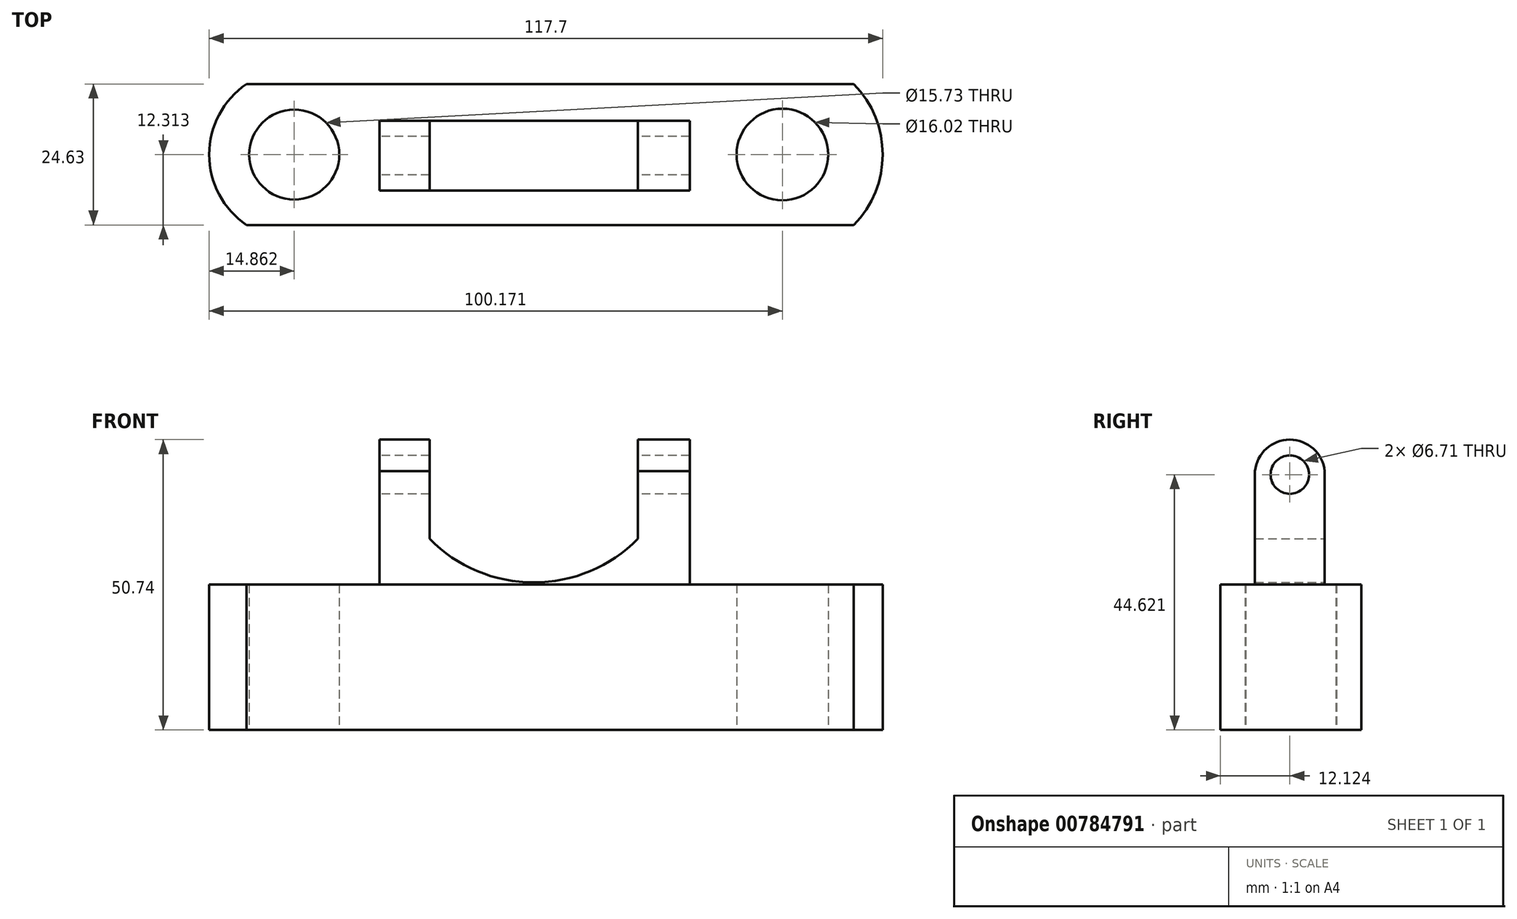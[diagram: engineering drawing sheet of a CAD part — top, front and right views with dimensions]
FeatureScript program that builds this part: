
annotation { "Feature Type Name" : "Feature", "Feature Type Description" : "" }
export const myFeature = defineFeature(function(context is Context, id is Id, definition is map)
    precondition{}
    {
        {
            var Q0;
            Q0=qCreatedBy(makeId("Top.planeOp"),FACE);
            var sketch = newSketch(context, id + "F0", { "sketchPlane" : qUnion([Q0])});
            skLineSegment(sketch, "E0", {"start": v(-47.53, -24.63) * mm, "end": v(58.57, -24.63) * mm});
            skLineSegment(sketch, "E1", {"start": v(-47.53, 0) * mm, "end": v(58.57, 0) * mm});
            skArc(sketch, "E2", {"start": v(-47.53, 0) * mm, "mid": v(-54.07, -12.32) * mm, "end": v(-47.53, -24.63) * mm});
            skArc(sketch, "E3", {"start": v(58.57, -24.63) * mm, "mid": v(63.63, -12.32) * mm, "end": v(58.57, 0) * mm});
            skCircle(sketch, "E4", {"center": v(-39.2, -12.32) * mm, "radius": 7.87 * mm});
            skCircle(sketch, "E5", {"center": v(46.1, -12.32) * mm, "radius": 8 * mm});
            skSolve(sketch);
        }
        {
            var Q0;
            Q0=makeQuery(id+"F0.imprint","IMPRINT",FACE,{"disambiguationData":[TD([[makeQuery(id+"F0.imprint","IMPRINT",EDGE,{"derivedFrom":sQuery(id+"F0.wireOp",EDGE,"E0")}),1.0]])]});
            extrude(context, id + "F1", {"entities" : qUnion([Q0]), "depth" : 25.4 * mm, "offsetDistance" : 25.4 * mm});
        }
        {
            var Q0;
            Q0=makeQuery(id+"F1.opExtrude","CAP_FACE",FACE,{"disambiguationData":[OSD([sQuery(id+"F0.wireOp",EDGE,"E0"),sQuery(id+"F0.wireOp",EDGE,"E1"),sQuery(id+"F0.wireOp",EDGE,"E2"),sQuery(id+"F0.wireOp",EDGE,"E3"),sQuery(id+"F0.wireOp",EDGE,"E4"),sQuery(id+"F0.wireOp",EDGE,"E5")])],"isStart":false});
            var sketch = newSketch(context, id + "F2", { "sketchPlane" : qUnion([Q0])});
            skLineSegment(sketch, "E6.bottom", {"start": v(-24.32, -6.42) * mm, "end": v(29.91, -6.42) * mm});
            skLineSegment(sketch, "E6.top", {"start": v(-24.32, -18.6) * mm, "end": v(29.91, -18.6) * mm});
            skLineSegment(sketch, "E6.left", {"start": v(-24.32, -6.42) * mm, "end": v(-24.32, -18.6) * mm});
            skLineSegment(sketch, "E6.right", {"start": v(29.91, -6.42) * mm, "end": v(29.91, -18.6) * mm});
            skSolve(sketch);
        }
        {
            var Q0;
            Q0=makeQuery(id+"F2.imprint","IMPRINT",FACE,{"disambiguationData":[TD([[makeQuery(id+"F2.imprint","IMPRINT",EDGE,{"derivedFrom":sQuery(id+"F2.wireOp",EDGE,"E6.bottom")}),-1.0]])]});
            extrude(context, id + "F3", {"entities" : qUnion([Q0]), "operationType" : NewBodyOperationType.ADD, "depth" : 25.4 * mm, "offsetDistance" : 25.4 * mm});
        }
        {
            var Q0;
            Q0=makeQuery(id+"F3.opExtrude","SWEPT_FACE",FACE,{"disambiguationData":[OSD([sQuery(id+"F2.wireOp",EDGE,"E6.bottom")])]});
            var sketch = newSketch(context, id + "F4", { "sketchPlane" : qUnion([Q0])});
            skLineSegment(sketch, "E7", {"start": v(-20.85, 50.8) * mm, "end": v(-20.85, 33.4) * mm});
            skLineSegment(sketch, "E8", {"start": v(15.55, 33.4) * mm, "end": v(15.55, 50.8) * mm});
            skArc(sketch, "E9", {"start": v(-20.85, 33.4) * mm, "mid": v(-2.65, 25.79) * mm, "end": v(15.55, 33.4) * mm});
            skSolve(sketch);
        }
        {
            var Q0;
            {var subQ0=sQuery(id+"F4.wireOp",EDGE,"E7");Q0=makeQuery(id+"F4.imprint","IMPRINT",FACE,{"disambiguationData":[TD([[makeQuery(id+"F4.imprint","IMPRINT",EDGE,{"derivedFrom":subQ0}),1.0]])]});}
            extrude(context, id + "F5", {"entities" : qUnion([Q0]), "operationType" : NewBodyOperationType.REMOVE, "oppositeDirection" : true, "depth" : 25.4 * mm, "offsetDistance" : 25.4 * mm});
        }
        {
            var Q0;
            Q0=makeQuery(id+"F3.opExtrude","SWEPT_FACE",FACE,{"disambiguationData":[OSD([sQuery(id+"F2.wireOp",EDGE,"E6.left")])]});
            var sketch = newSketch(context, id + "F6", { "sketchPlane" : qUnion([Q0])});
            skArc(sketch, "E10", {"start": v(18.6, 45.22) * mm, "mid": v(12.5, 50.74) * mm, "end": v(6.42, 45.22) * mm});
            skCircle(sketch, "E11", {"center": v(12.5, 44.62) * mm, "radius": 3.35 * mm});
            skSolve(sketch);
        }
        {
            var Q0;
            {var subQ0=sQuery(id+"F6.wireOp",EDGE,"E10");Q0=makeQuery(id+"F6.imprint","IMPRINT",FACE,{"disambiguationData":[TD([[makeQuery(id+"F6.imprint","IMPRINT",EDGE,{"derivedFrom":subQ0}),-1.0]])]});}
            var Q1;
            Q1=makeQuery(id+"F6.imprint","IMPRINT",FACE,{"disambiguationData":[TD([[makeQuery(id+"F6.imprint","IMPRINT",EDGE,{"derivedFrom":sQuery(id+"F6.wireOp",EDGE,"E11")}),1.0]])]});
            extrude(context, id + "F7", {"entities" : qUnion([Q0, Q1]), "operationType" : NewBodyOperationType.REMOVE, "oppositeDirection" : true, "depth" : 77.98 * mm, "offsetDistance" : 25.4 * mm});
        }
    });
